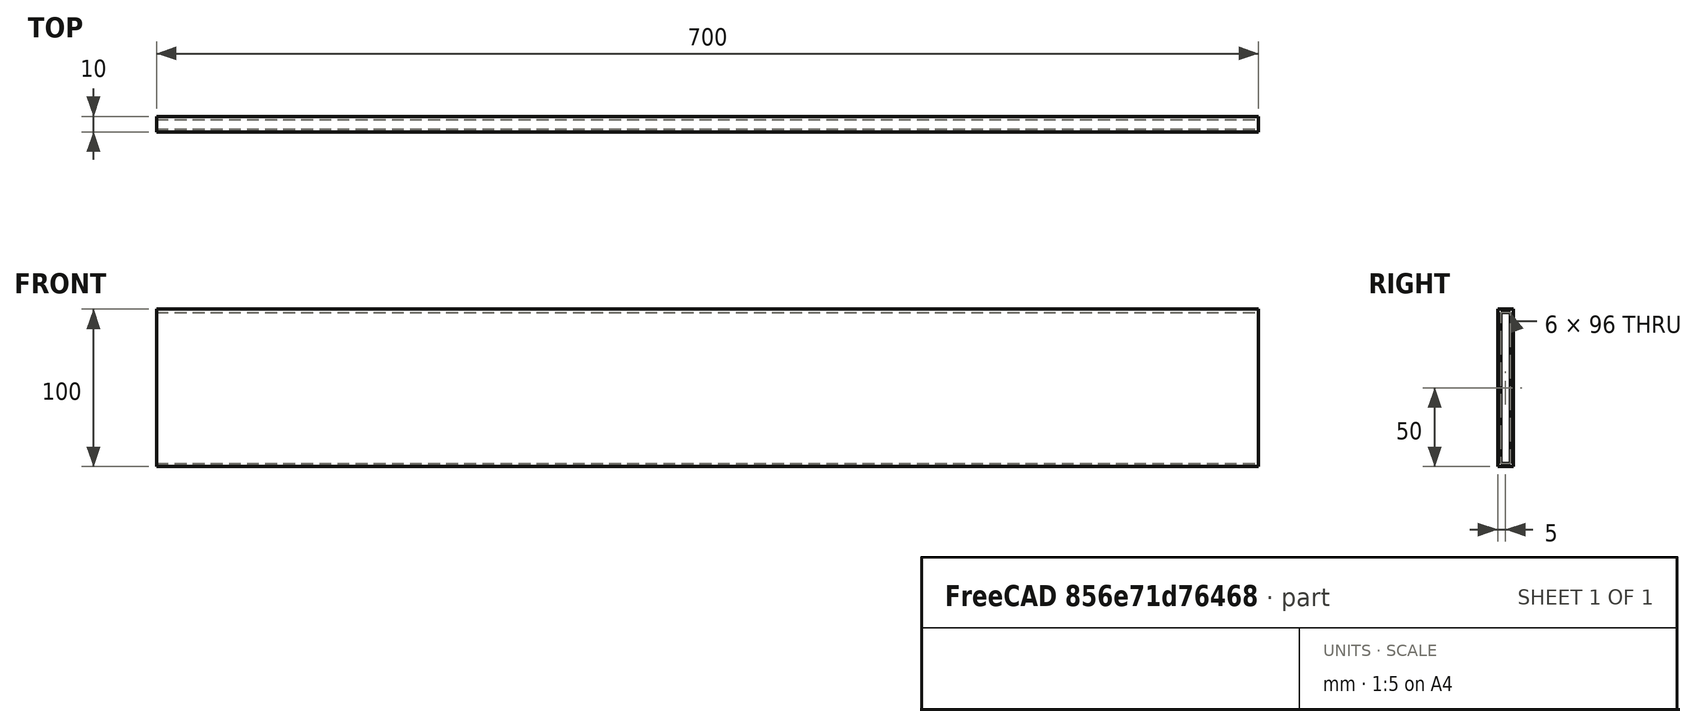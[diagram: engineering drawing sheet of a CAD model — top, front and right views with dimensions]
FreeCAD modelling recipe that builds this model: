
FCSTD DOCUMENT  (FreeCAD 0.20R29410 (Git))
Label: littleSling
License: All rights reserved
LicenseURL: http://en.wikipedia.org/wiki/All_rights_reserved
objects: Sketcher::SketchObject×1, PartDesign::Pad×1, PartDesign::Body×1
note: 4 computed .brp shape members not serialized (recipe doc carries the construction recipe); baked Part::Feature solids carry a one-line shape summary decoded from their .brp

FEATURE [Sketcher::SketchObject] Sketch
  FullyConstrained = true
  MapMode = 5
  Placement = pos=(0,0,0) rot=(0.57735,0.57735,0.57735;2.0944rad)
  Support = -> [YZ_Plane001]
  sketch-geometry (8):
    g0: LineSegment StartX=0 StartY=0 StartZ=0 EndX=10 EndY=0 EndZ=0
    g1: LineSegment StartX=10 StartY=0 StartZ=0 EndX=10 EndY=-100 EndZ=0
    g2: LineSegment StartX=10 StartY=-100 StartZ=0 EndX=0 EndY=-100 EndZ=0
    g3: LineSegment StartX=0 StartY=-100 StartZ=0 EndX=0 EndY=0 EndZ=0
    g4: LineSegment StartX=2 StartY=-2 StartZ=0 EndX=8 EndY=-2 EndZ=0
    g5: LineSegment StartX=8 StartY=-2 StartZ=0 EndX=8 EndY=-98 EndZ=0
    g6: LineSegment StartX=8 StartY=-98 StartZ=0 EndX=2 EndY=-98 EndZ=0
    g7: LineSegment StartX=2 StartY=-98 StartZ=0 EndX=2 EndY=-2 EndZ=0
  constraints (23):
    c: Coincident(g0,g1)
    c: Coincident(g1,g2)
    c: Coincident(g2,g3)
    c: Coincident(g3,g0)
    c: Horizontal(g0)
    c: Horizontal(g2)
    c: Vertical(g1)
    c: Vertical(g3)
    c: Coincident(g0,g-1)
    c: Coincident(g4,g5)
    c: Coincident(g5,g6)
    c: Coincident(g6,g7)
    c: Coincident(g7,g4)
    c: Horizontal(g4)
    c: Horizontal(g6)
    c: Vertical(g5)
    c: Vertical(g7)
    c: DistanceY(g3,g3) = 100
    c: DistanceX(g2,g2) = 10
    c: DistanceX(g2,g6) = 2
    c: DistanceY(g4,g0) = 2
    c: DistanceX(g5,g1) = 2
    c: DistanceY(g2,g6) = 2
FEATURE [PartDesign::Pad] Pad
  Direction = (1,-2e-16,3e-16)
  Length = 700
  Length2 = 10
  Placement = pos=(0,0,0) rot=(0.57735,0.57735,0.57735;2.0944rad)
  Profile = -> Sketch
  ReferenceAxis = -> Sketch [N_Axis]
  Type = 0
FEATURE [PartDesign::Body] Body001
  Group = -> [Sketch,Pad]
  Origin = -> Origin001
  Tip = -> Pad
